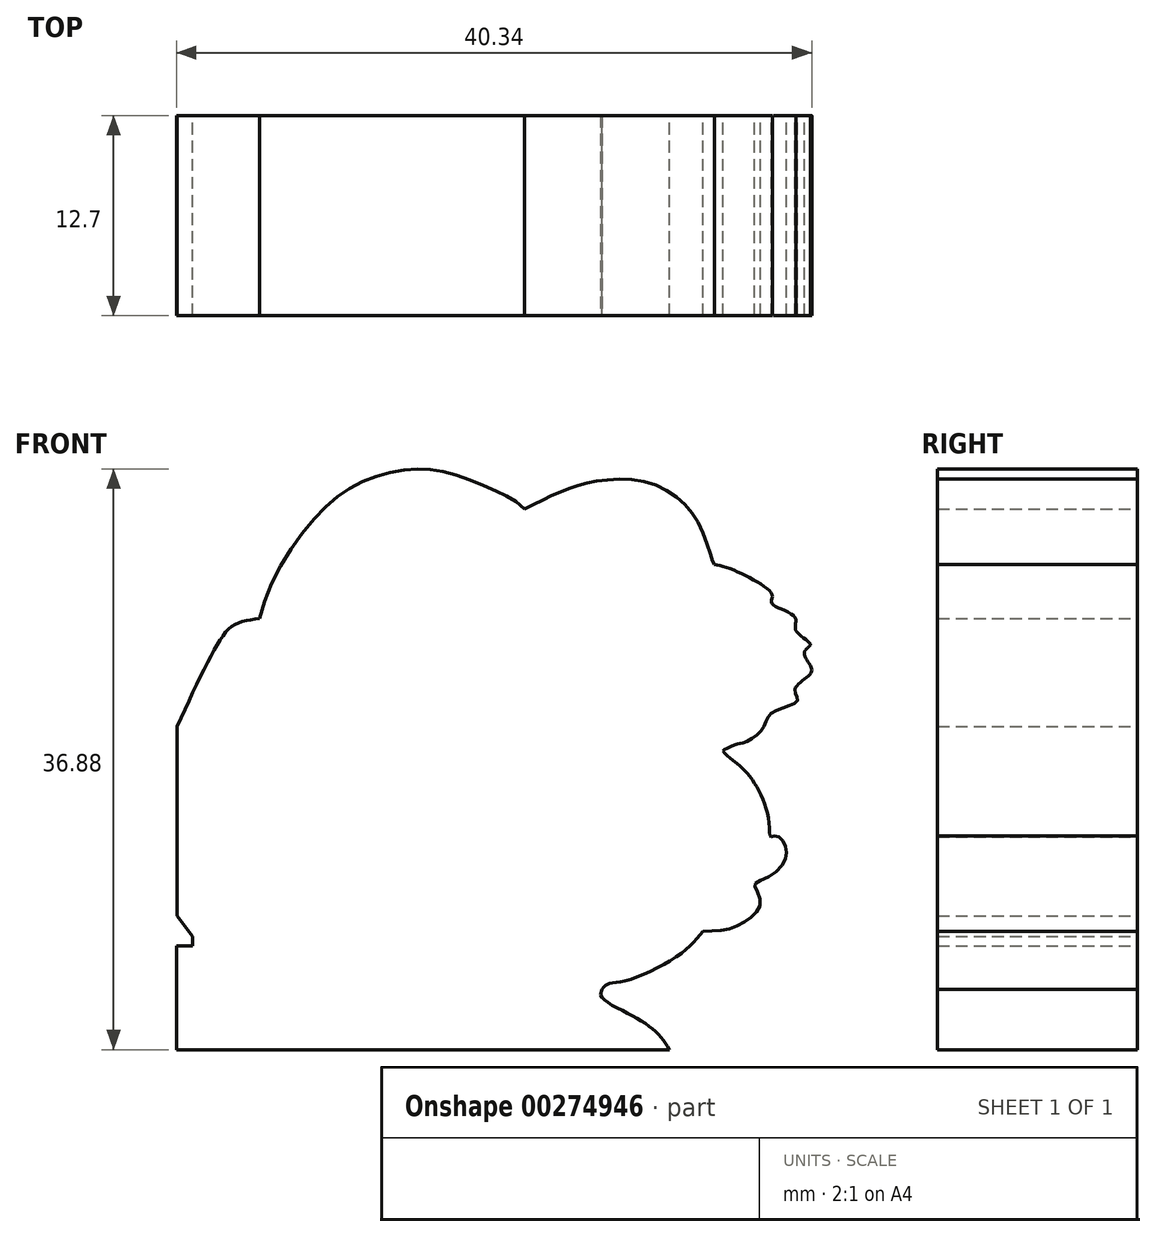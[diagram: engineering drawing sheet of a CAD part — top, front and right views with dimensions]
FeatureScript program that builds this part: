
annotation { "Feature Type Name" : "Feature", "Feature Type Description" : "" }
export const myFeature = defineFeature(function(context is Context, id is Id, definition is map)
    precondition{}
    {
        {
            var Q0;
            Q0=qCreatedBy(makeId("Front.planeOp"),FACE);
            var sketch = newSketch(context, id + "F0", { "sketchPlane" : qUnion([Q0])});
            skFitSpline(sketch, "E0", {"points": [v(-15.62, 5.1) * mm, v(-14.7, 9.75) * mm, v(-11.6, 14.7) * mm, v(-8.67, 16.94) * mm, v(-5.56, 17.74) * mm, v(-2.92, 17.45) * mm, v(0, 16.3) * mm, v(1.68, 15.21) * mm, v(3, 12.57) * mm, v(3, 11.7) * mm], "startDerivative": vector(3.37, 33.21) * mm, "endDerivative": vector(-2.08, -12.11) * mm});
            skFitSpline(sketch, "E1", {"points": [v(-15.15, 8.27) * mm, v(-16.66, 7.91) * mm, v(-17.8, 6.67) * mm, v(-20.39, 1.42) * mm], "startDerivative": vector(-6.49, -0.82) * mm, "endDerivative": vector(-5.81, -12.52) * mm});
            skLineSegment(sketch, "E2", {"start": v(-20.39, 1.42) * mm, "end": v(-20.39, -10.63) * mm});
            skLineSegment(sketch, "E3", {"start": v(-20.39, -10.63) * mm, "end": v(-19.4, -11.9) * mm});
            skLineSegment(sketch, "E4", {"start": v(-19.4, -11.9) * mm, "end": v(-19.4, -12.54) * mm});
            skLineSegment(sketch, "E5", {"start": v(-19.4, -12.54) * mm, "end": v(-20.42, -12.54) * mm});
            skFitSpline(sketch, "E6", {"points": [v(-19.4, -11.9) * mm, v(-16.63, -13.36) * mm, v(-12.46, -14.63) * mm, v(-4.97, -15.57) * mm, v(1.91, -15.72) * mm, v(5.72, -15.28) * mm], "startDerivative": vector(16.85, -9.64) * mm, "endDerivative": vector(20.19, 3.05) * mm});
            skFitSpline(sketch, "E7", {"points": [v(5.72, -15.28) * mm, v(6.6, -15.28) * mm, v(6.5, -15.63) * mm, v(8.19, -16.8) * mm, v(10.04, -18) * mm, v(10.9, -19.12) * mm], "startDerivative": vector(7.56, 0.96) * mm, "endDerivative": vector(3.56, -5.5) * mm});
            skFitSpline(sketch, "E8", {"points": [v(13.01, -11.61) * mm, v(11.42, -13.15) * mm, v(7.94, -14.79) * mm, v(6.96, -14.95) * mm, v(6.6, -15.28) * mm], "startDerivative": vector(-4.35, -5.24) * mm, "endDerivative": vector(-2.34, -2.9) * mm});
            skFitSpline(sketch, "E9", {"points": [v(13.01, -11.61) * mm, v(14.76, -11.42) * mm, v(16.07, -10.7) * mm, v(16.66, -9.76) * mm, v(16.3, -8.77) * mm, v(16.37, -8.55) * mm, v(17.65, -7.83) * mm, v(18.3, -6.7) * mm, v(18.13, -5.95) * mm, v(17.65, -5.54) * mm, v(17.35, -5.6) * mm, v(17.17, -4.4) * mm, v(16.53, -2.63) * mm, v(15.57, -1.3) * mm, v(14.3, -0.14) * mm, v(14.5, 0) * mm, v(15.19, 0.3) * mm, v(15.55, 0.36) * mm, v(16.76, 1.21) * mm, v(17.4, 2.28) * mm, v(19, 3.04) * mm, v(18.86, 3.77) * mm, v(19.83, 4.75) * mm, v(19.8, 5.32) * mm, v(19.47, 6.18) * mm, v(19.83, 6.63) * mm, v(18.92, 7.49) * mm, v(18.86, 8.34) * mm, v(17.4, 9.22) * mm, v(17.43, 9.7) * mm, v(15.86, 10.91) * mm, v(13.74, 11.69) * mm, v(13.01, 11.63) * mm, v(12.16, 11.92) * mm, v(11.12, 11.77) * mm], "startDerivative": vector(47.52, 1.52) * mm, "endDerivative": vector(-35.8, -10.38) * mm});
            skFitSpline(sketch, "E10", {"points": [v(1.68, 15.21) * mm, v(3.37, 16.06) * mm, v(4.86, 16.64) * mm, v(6.56, 17.03) * mm, v(9.23, 16.99) * mm, v(11.56, 15.8) * mm, v(12.91, 13.97) * mm, v(13.58, 12.04) * mm, v(13.74, 11.69) * mm], "startDerivative": vector(13.42, 7.03) * mm, "endDerivative": vector(2.5, -4.63) * mm});
            skFitSpline(sketch, "E11", {"points": [v(3, 11.7) * mm, v(5.46, 11.94) * mm, v(8.02, 12.12) * mm, v(11.12, 11.77) * mm], "startDerivative": vector(7.74, 0.7) * mm, "endDerivative": vector(8.89, -1.38) * mm});
            skFitSpline(sketch, "E12", {"points": [v(3, 11.7) * mm, v(2.66, 11.63) * mm, v(2.2, 11.92) * mm, v(0, 12.89) * mm, v(-2.11, 13.42) * mm, v(-4.22, 13.46) * mm, v(-6.09, 13.13) * mm, v(-7.5, 12.52) * mm, v(-9.14, 11.46) * mm], "startDerivative": vector(-5.87, -2.32) * mm, "endDerivative": vector(-11.78, -8.1) * mm});
            skFitSpline(sketch, "E13", {"points": [v(5.72, 7.97) * mm, v(5.99, 8.43) * mm, v(5.96, 8.81) * mm, v(2.66, 11.63) * mm], "startDerivative": vector(1.5, 2.26) * mm, "endDerivative": vector(-7.4, 5.65) * mm});
            skFitSpline(sketch, "E14", {"points": [v(5.06, 9.74) * mm, v(2.66, 10.09) * mm, v(0, 10.12) * mm, v(-3.4, 9.5) * mm, v(-4.6, 9.06) * mm, v(-5.95, 8.05) * mm, v(-7.66, 7.43) * mm, v(-8.6, 7.21) * mm], "startDerivative": vector(-15.14, 2.5) * mm, "endDerivative": vector(-8.64, -1.87) * mm});
            skFitSpline(sketch, "E15", {"points": [v(5.72, 7.97) * mm, v(3.76, 8.68) * mm, v(1.16, 9.06) * mm, v(-1.26, 8.98) * mm, v(-3.78, 7.97) * mm, v(-5.49, 7.02) * mm, v(-7.47, 6.35) * mm, v(-9.72, 6.18) * mm, v(-10.02, 5.59) * mm, v(-9.7, 5.07) * mm, v(-8.74, 5.07) * mm, v(-7.66, 4.93) * mm, v(-6.36, 4.07) * mm, v(-4.05, 2.98) * mm, v(-2.26, 2.33) * mm, v(1.57, 2.28) * mm, v(6.18, 3.74) * mm, v(6.86, 5.78) * mm, v(6.26, 6.86) * mm, v(3.11, 7.76) * mm, v(0.83, 8.2) * mm, v(-0.9, 7.97) * mm, v(-3.26, 7.43) * mm, v(-5.27, 6.37) * mm, v(-7.22, 4.77) * mm], "startDerivative": vector(-44.4, 18.77) * mm, "endDerivative": vector(-42.04, -36.8) * mm});
            skFitSpline(sketch, "E16", {"points": [v(5.99, 8.43) * mm, v(9.85, 9.55) * mm, v(13.44, 9.8) * mm, v(17.4, 9.22) * mm], "startDerivative": vector(11.47, 3.81) * mm, "endDerivative": vector(11.84, -2.2) * mm});
            skFitSpline(sketch, "E17", {"points": [v(6.22, 7.63) * mm, v(8.63, 8.43) * mm, v(11.64, 8.81) * mm, v(15.03, 8.67) * mm, v(17.05, 8.2) * mm, v(19.83, 6.63) * mm], "startDerivative": vector(12.4, 4.73) * mm, "endDerivative": vector(13.74, -8.6) * mm});
            skFitSpline(sketch, "E18", {"points": [v(6.86, 5.78) * mm, v(8.64, 6.85) * mm, v(10.7, 7.49) * mm, v(12.3, 7.97) * mm, v(16.84, 7.23) * mm, v(17.4, 6.63) * mm, v(18.08, 6.63) * mm, v(19.47, 6.18) * mm], "startDerivative": vector(10.75, 7.75) * mm, "endDerivative": vector(11.2, -5.1) * mm});
            skFitSpline(sketch, "E19", {"points": [v(6.18, 3.74) * mm, v(6.53, 3.43) * mm, v(7.4, 3.02) * mm, v(10.51, 2.66) * mm, v(12.67, 2.6) * mm, v(16.16, 3.07) * mm, v(18.86, 3.77) * mm], "startDerivative": vector(4, -3.78) * mm, "endDerivative": vector(12.77, 3.74) * mm});
            skFitSpline(sketch, "E20", {"points": [v(6.53, 3.43) * mm, v(6.4, 2.7) * mm, v(5.07, 1.63) * mm, v(4.33, 1.62) * mm, v(3.03, 1.12) * mm, v(-2.74, 1.42) * mm, v(-6.87, 2.98) * mm], "startDerivative": vector(0.5, -6.93) * mm, "endDerivative": vector(-15.2, 7.28) * mm});
            skFitSpline(sketch, "E21", {"points": [v(3.76, 0.67) * mm, v(2.66, 0.28) * mm, v(1.87, 0) * mm, v(-1.61, -1.5) * mm], "startDerivative": vector(-4.35, -1.55) * mm, "endDerivative": vector(-8.4, -3.68) * mm});
            skFitSpline(sketch, "E22", {"points": [v(7.36, 0.28) * mm, v(9.62, -0.56) * mm, v(10.49, -1.3) * mm], "startDerivative": vector(4.31, -1.3) * mm, "endDerivative": vector(1.8, -1.9) * mm});
            skFitSpline(sketch, "E23", {"points": [v(14.3, -0.14) * mm, v(12.47, -0.52) * mm, v(9.62, -0.56) * mm], "startDerivative": vector(-3.85, -1.02) * mm, "endDerivative": vector(-5.46, 0.15) * mm});
            skFitSpline(sketch, "E24", {"points": [v(17.35, -5.6) * mm, v(15.57, -6.28) * mm, v(12.67, -7.18) * mm, v(9.62, -7.47) * mm, v(6.86, -7.33) * mm, v(0, -6.35) * mm, v(-4.49, -5.6) * mm, v(-7.16, -5.6) * mm, v(-8.54, -5.91) * mm, v(-9.63, -7.14) * mm, v(-9.99, -8.3) * mm, v(-9.74, -9.14) * mm, v(-8.87, -9.75) * mm, v(-5.4, -9.82) * mm, v(0, -10.77) * mm, v(4.93, -11.35) * mm, v(13.01, -11.61) * mm], "startDerivative": vector(-33.6, -12.74) * mm, "endDerivative": vector(84.35, -1.87) * mm});
            skFitSpline(sketch, "E25", {"points": [v(-11.47, -9.46) * mm, v(-11.18, -10.44) * mm, v(-10.71, -10.98) * mm, v(-9.6, -11.53) * mm, v(-8.65, -11.67) * mm], "startDerivative": vector(0.95, -4.18) * mm, "endDerivative": vector(3.65, -0.27) * mm});
            skFitSpline(sketch, "E26", {"points": [v(-19.4, -12.54) * mm, v(-18.23, -13.47) * mm, v(-16.09, -14.6) * mm, v(-13.21, -15.57) * mm, v(-10.93, -16.34) * mm, v(-6.05, -16.8) * mm, v(0, -17.12) * mm, v(3.94, -16.7) * mm, v(5.54, -16.02) * mm, v(6.14, -15.23) * mm], "startDerivative": vector(13.3, -11.37) * mm, "endDerivative": vector(7.42, 12.74) * mm});
            skLineSegment(sketch, "E27", {"start": v(-20.42, -12.54) * mm, "end": v(-20.42, -19.12) * mm});
            skLineSegment(sketch, "E28", {"start": v(-20.42, -19.12) * mm, "end": v(10.9, -19.12) * mm});
            skSolve(sketch);
        }
        {
            var Q0;
            Q0 = qSketchRegion(id + "F0", true);
            extrude(context, id + "F1", {"entities" : qUnion([Q0]), "depth" : 12.7 * mm});
        }
    });
